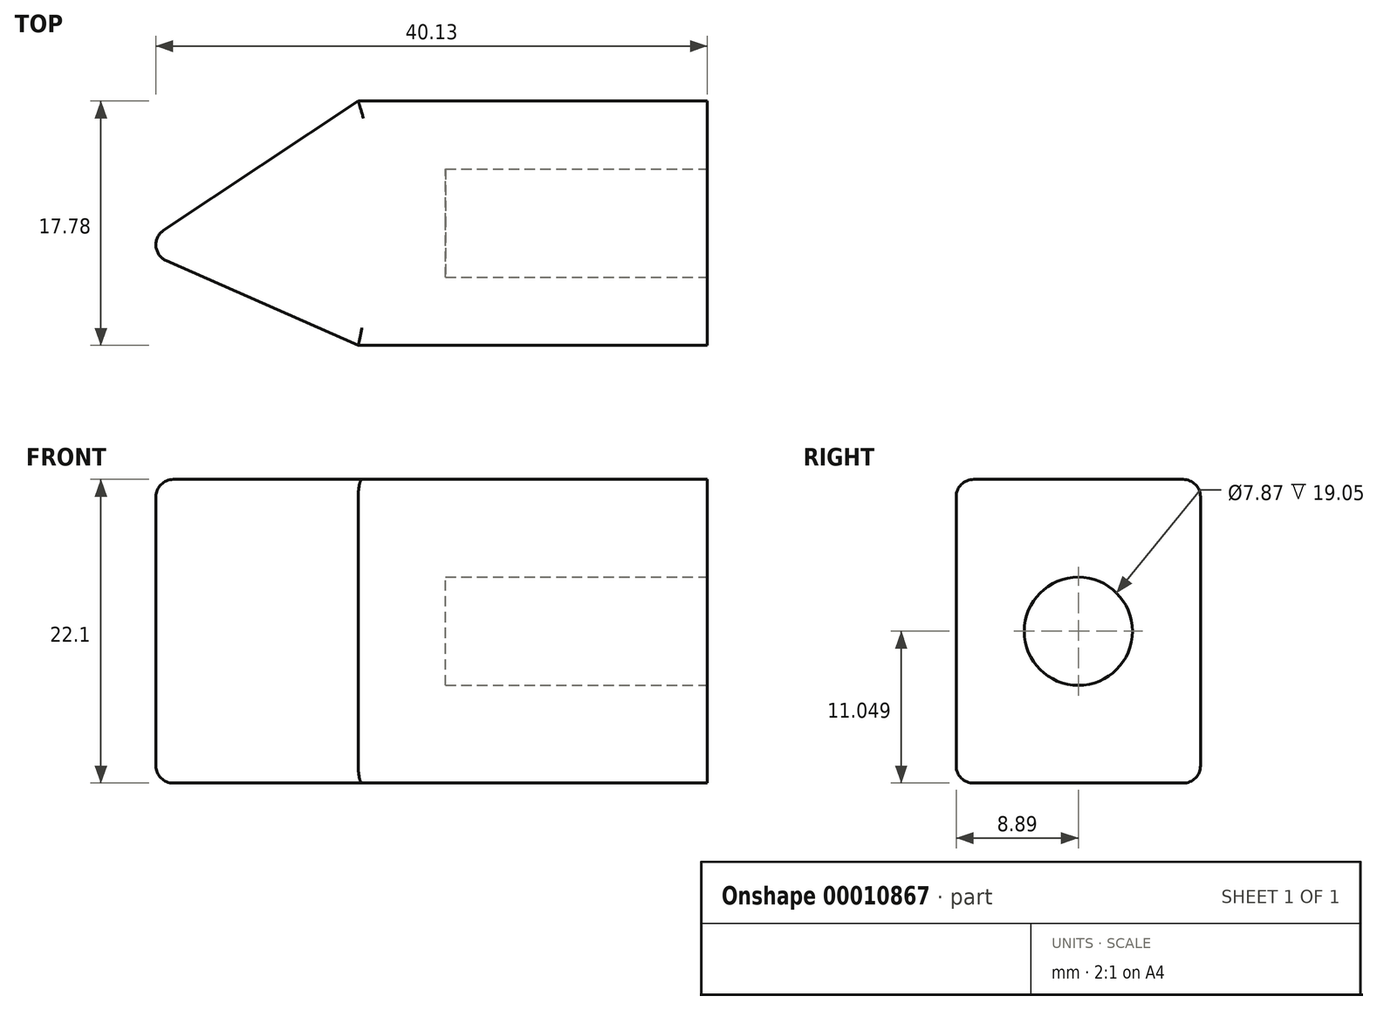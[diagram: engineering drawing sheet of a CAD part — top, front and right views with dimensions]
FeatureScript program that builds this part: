
annotation { "Feature Type Name" : "Feature", "Feature Type Description" : "" }
export const myFeature = defineFeature(function(context is Context, id is Id, definition is map)
    precondition{}
    {
        {
            var Q0;
            Q0=qCreatedBy(makeId("Top.planeOp"),FACE);
            var sketch = newSketch(context, id + "F0", { "sketchPlane" : qUnion([Q0])});
            skLineSegment(sketch, "E0.bottom", {"start": v(3.05, 0) * mm, "end": v(28.45, 0) * mm});
            skLineSegment(sketch, "E0.top", {"start": v(3.05, 17.78) * mm, "end": v(28.45, 17.78) * mm});
            skLineSegment(sketch, "E0.left", {"start": v(3.05, 0) * mm, "end": v(3.05, 17.78) * mm});
            skLineSegment(sketch, "E0.right", {"start": v(28.45, 0) * mm, "end": v(28.45, 17.78) * mm});
            skLineSegment(sketch, "E1", {"start": v(3.05, 0) * mm, "end": v(-13.05, 7.1) * mm});
            skLineSegment(sketch, "E2", {"start": v(-13.05, 7.1) * mm, "end": v(3.05, 17.78) * mm});
            skSolve(sketch);
        }
        {
            var Q0;
            Q0=makeQuery(id+"F0.imprint","IMPRINT",FACE,{"disambiguationData":[TD([[makeQuery(id+"F0.imprint","IMPRINT",EDGE,{"derivedFrom":sQuery(id+"F0.wireOp",EDGE,"E0.bottom")}),1.0]])]});
            var Q1;
            Q1=makeQuery(id+"F0.imprint","IMPRINT",FACE,{"disambiguationData":[TD([[makeQuery(id+"F0.imprint","IMPRINT",EDGE,{"derivedFrom":sQuery(id+"F0.wireOp",EDGE,"E0.left")}),1.0]])]});
            extrude(context, id + "F1", {"entities" : qUnion([Q0, Q1]), "depth" : 22.1 * mm});
        }
        {
            var Q0;
            Q0=makeQuery(id+"F1.opExtrude","SWEPT_FACE",FACE,{"disambiguationData":[OSD([sQuery(id+"F0.wireOp",EDGE,"E0.right")])]});
            var sketch = newSketch(context, id + "F2", { "sketchPlane" : qUnion([Q0])});
            skCircle(sketch, "E3", {"center": v(8.89, 11.05) * mm, "radius": 3.94 * mm});
            skPoint(sketch, "E3.centerSnap0", {"position": v(8.89, 0) * mm});
            skPoint(sketch, "E3.centerSnap1", {"position": v(17.78, 11.05) * mm});
            skSolve(sketch);
        }
        {
            var Q0;
            Q0=makeQuery(id+"F2.imprint","IMPRINT",FACE,{"disambiguationData":[TD([[makeQuery(id+"F2.imprint","IMPRINT",EDGE,{"derivedFrom":sQuery(id+"F2.wireOp",EDGE,"E3")}),1.0]])]});
            extrude(context, id + "F3", {"entities" : qUnion([Q0]), "operationType" : NewBodyOperationType.REMOVE, "oppositeDirection" : true, "depth" : 19.05 * mm});
        }
        {
            var Q0;
            Q0=makeQuery(id+"F1.opExtrude","CAP_EDGE",EDGE,{"disambiguationData":[OSD([sQuery(id+"F0.wireOp",EDGE,"E2")])],"isStart":false});
            var Q1;
            Q1=makeQuery(id+"F1.opExtrude","SWEPT_EDGE",EDGE,{"disambiguationData":[OSD([sQuery(id+"F0.wireOp",EDGE,"E1"),sQuery(id+"F0.wireOp",EDGE,"E2")])]});
            var Q2;
            Q2=makeQuery(id+"F1.opExtrude","CAP_EDGE",EDGE,{"disambiguationData":[OSD([sQuery(id+"F0.wireOp",EDGE,"E2")])],"isStart":true});
            var Q3;
            Q3=makeQuery(id+"F1.opExtrude","CAP_EDGE",EDGE,{"disambiguationData":[OSD([sQuery(id+"F0.wireOp",EDGE,"E0.top")])],"isStart":true});
            var Q4;
            Q4=makeQuery(id+"F1.opExtrude","CAP_EDGE",EDGE,{"disambiguationData":[OSD([sQuery(id+"F0.wireOp",EDGE,"E0.top")])],"isStart":false});
            var Q5;
            Q5=makeQuery(id+"F1.opExtrude","CAP_EDGE",EDGE,{"disambiguationData":[OSD([sQuery(id+"F0.wireOp",EDGE,"E1")])],"isStart":false});
            var Q6;
            Q6=makeQuery(id+"F1.opExtrude","CAP_EDGE",EDGE,{"disambiguationData":[OSD([sQuery(id+"F0.wireOp",EDGE,"E0.bottom")])],"isStart":false});
            var Q7;
            Q7=makeQuery(id+"F1.opExtrude","CAP_EDGE",EDGE,{"disambiguationData":[OSD([sQuery(id+"F0.wireOp",EDGE,"E1")])],"isStart":true});
            var Q8;
            Q8=makeQuery(id+"F1.opExtrude","CAP_EDGE",EDGE,{"disambiguationData":[OSD([sQuery(id+"F0.wireOp",EDGE,"E0.bottom")])],"isStart":true});
            fillet(context, id + "F4", {"entities" : qUnion([Q0, Q1, Q2, Q3, Q4, Q5, Q6, Q7, Q8]), "radius" : 1.27 * mm, "tangentPropagation" : true, "allowEdgeOverflow" : false});
        }
    });
